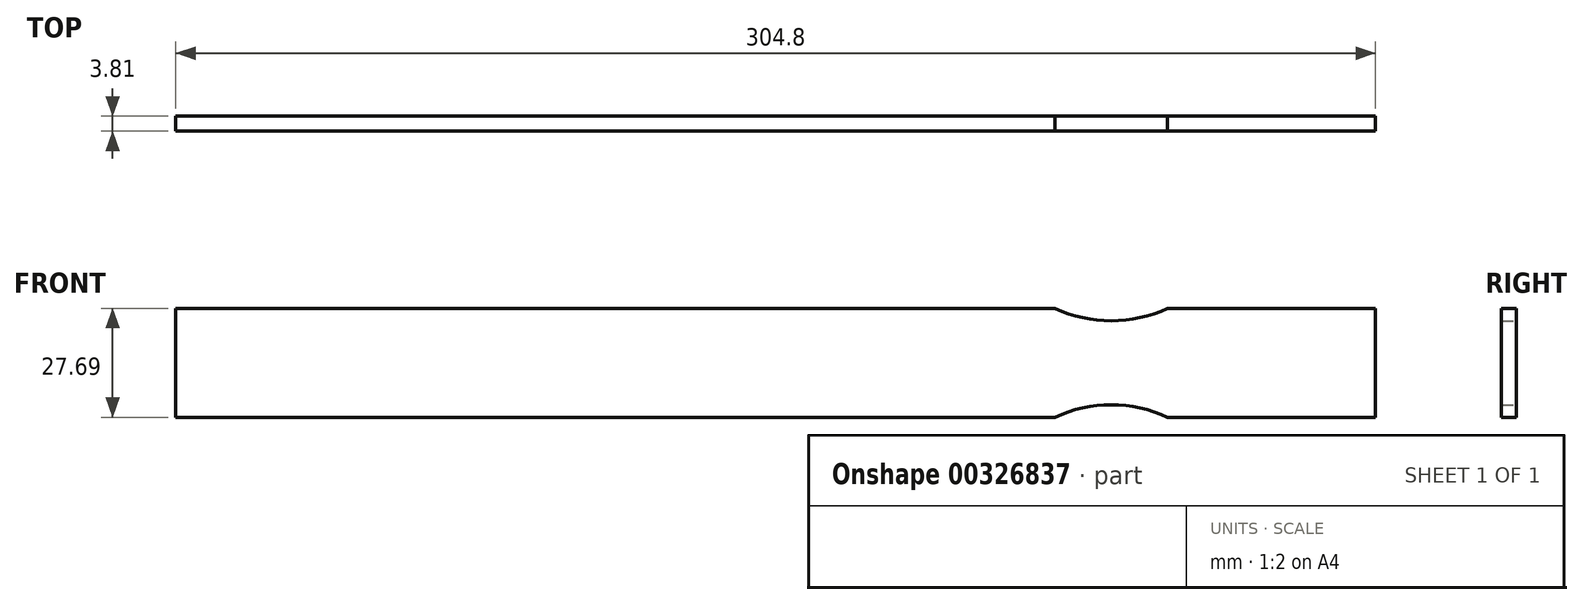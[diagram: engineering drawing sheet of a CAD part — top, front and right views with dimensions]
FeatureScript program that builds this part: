
annotation { "Feature Type Name" : "Feature", "Feature Type Description" : "" }
export const myFeature = defineFeature(function(context is Context, id is Id, definition is map)
    precondition{}
    {
        {
            var Q0;
            Q0=qCreatedBy(makeId("Front.planeOp"),FACE);
            var sketch = newSketch(context, id + "F0", { "sketchPlane" : qUnion([Q0])});
            skLineSegment(sketch, "E0.bottom", {"start": v(0, 0) * mm, "end": v(223.4, 0) * mm});
            skLineSegment(sketch, "E0.top", {"start": v(0, 27.69) * mm, "end": v(223.4, 27.69) * mm});
            skLineSegment(sketch, "E0.left", {"start": v(0, 0) * mm, "end": v(0, 27.69) * mm});
            skLineSegment(sketch, "E0.right", {"start": v(304.8, 0) * mm, "end": v(304.8, 27.69) * mm});
            skArc(sketch, "E1", {"start": v(223.4, 27.69) * mm, "mid": v(237.68, 24.51) * mm, "end": v(251.97, 27.69) * mm});
            skArc(sketch, "E2", {"start": v(251.97, 0) * mm, "mid": v(237.68, 3.18) * mm, "end": v(223.4, 0) * mm});
            skLineSegment(sketch, "E3.trimOffspring", {"start": v(251.97, 27.69) * mm, "end": v(304.8, 27.69) * mm});
            skLineSegment(sketch, "E4.trimOffspring", {"start": v(251.97, 0) * mm, "end": v(304.8, 0) * mm});
            skSolve(sketch);
        }
        {
            var Q0;
            Q0=makeQuery(id+"F0.imprint","IMPRINT",FACE,{"disambiguationData":[TD([[makeQuery(id+"F0.imprint","IMPRINT",EDGE,{"derivedFrom":sQuery(id+"F0.wireOp",EDGE,"E0.bottom")}),1.0]])]});
            extrude(context, id + "F1", {"entities" : qUnion([Q0]), "depth" : 3.8 * mm});
        }
    });
